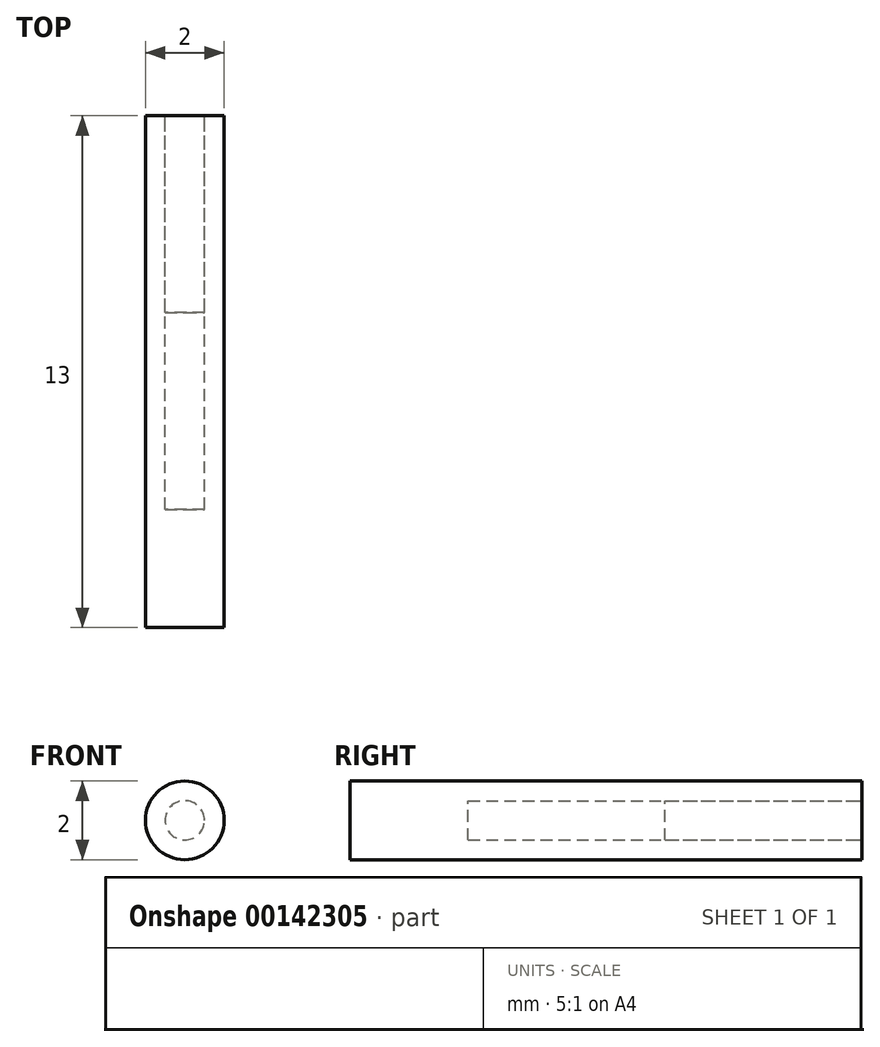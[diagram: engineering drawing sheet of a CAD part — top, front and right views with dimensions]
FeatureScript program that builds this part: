
annotation { "Feature Type Name" : "Feature", "Feature Type Description" : "" }
export const myFeature = defineFeature(function(context is Context, id is Id, definition is map)
    precondition{}
    {
        {
            var Q0;
            Q0=qCreatedBy(makeId("Front.planeOp"),FACE);
            var sketch = newSketch(context, id + "F0", { "sketchPlane" : qUnion([Q0])});
            skCircle(sketch, "E0", {"center": v(0, 0) * mm, "radius": 1 * mm});
            skSolve(sketch);
        }
        {
            var Q0;
            Q0 = qSketchRegion(id + "F0", true);
            extrude(context, id + "F1", {"entities" : qUnion([Q0]), "depth" : 13 * mm});
        }
        {
            var Q0;
            Q0=qCreatedBy(makeId("Front.planeOp"),FACE);
            var sketch = newSketch(context, id + "F2", { "sketchPlane" : qUnion([Q0])});
            skCircle(sketch, "E1", {"center": v(0, 0) * mm, "radius": 0.5 * mm});
            skSolve(sketch);
        }
        {
            var Q0;
            Q0 = qSketchRegion(id + "F2", true);
            extrude(context, id + "F3", {"entities" : qUnion([Q0]), "depth" : 5 * mm});
        }
        {
            var Q0;
            Q0 = qSketchRegion(id + "F2", true);
            extrude(context, id + "F4", {"entities" : qUnion([Q0]), "depth" : 10 * mm});
        }
    });
